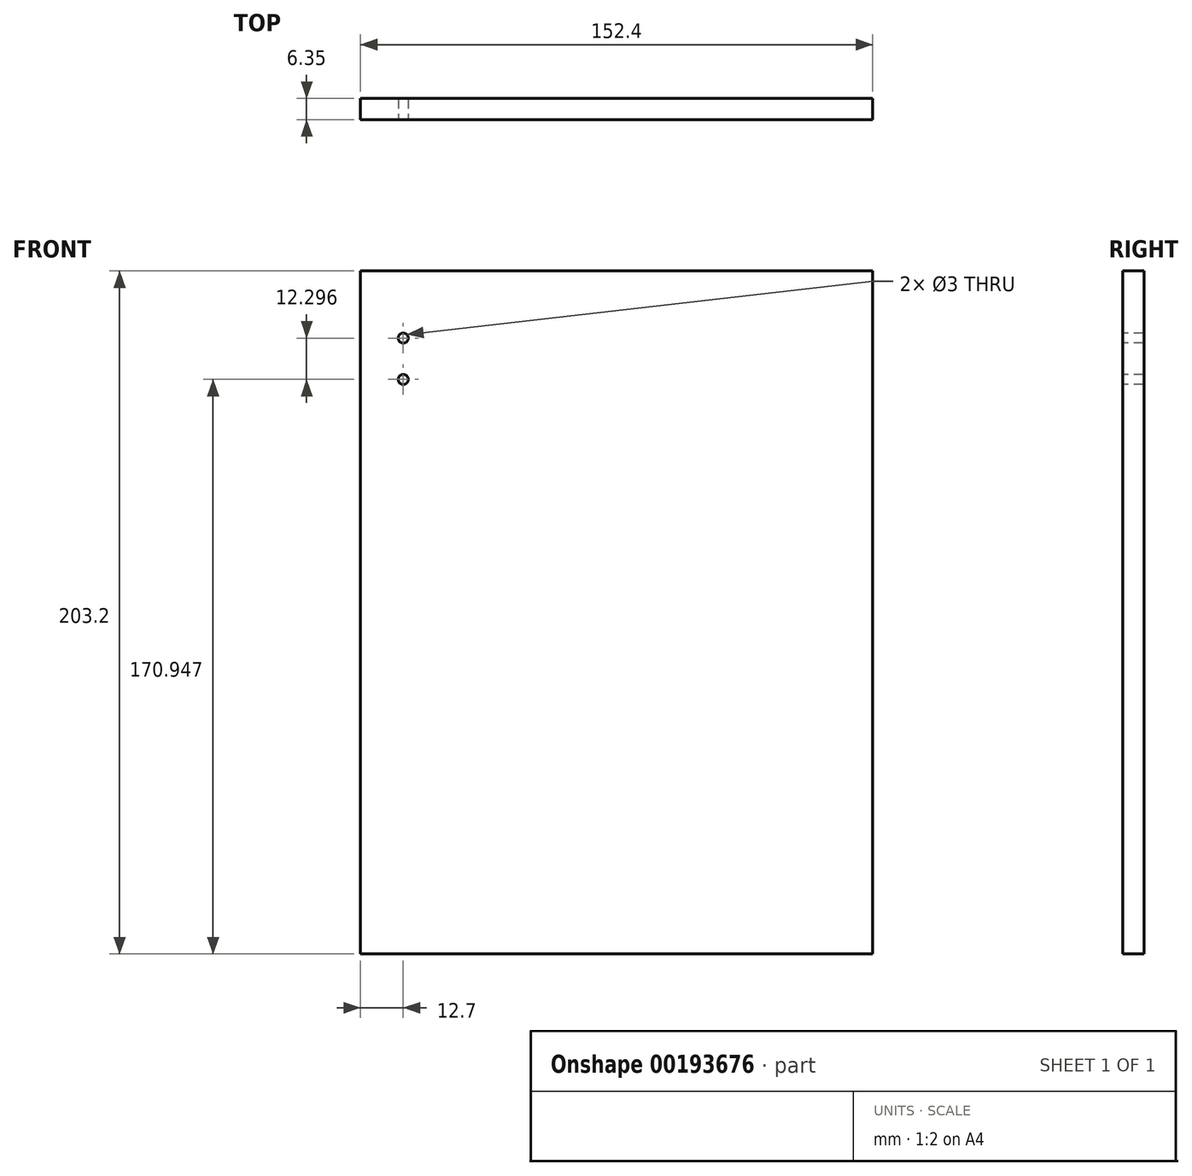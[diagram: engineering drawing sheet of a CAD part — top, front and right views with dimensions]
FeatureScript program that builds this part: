
annotation { "Feature Type Name" : "Feature", "Feature Type Description" : "" }
export const myFeature = defineFeature(function(context is Context, id is Id, definition is map)
    precondition{}
    {
        {
            var Q0;
            Q0=qCreatedBy(makeId("Front.planeOp"),FACE);
            var sketch = newSketch(context, id + "F0", { "sketchPlane" : qUnion([Q0])});
            skLineSegment(sketch, "E0.bottom", {"start": v(76.2, 101.6) * mm, "end": v(-76.2, 101.6) * mm});
            skLineSegment(sketch, "E0.top", {"start": v(76.2, -101.6) * mm, "end": v(-76.2, -101.6) * mm});
            skLineSegment(sketch, "E0.left", {"start": v(76.2, 101.6) * mm, "end": v(76.2, -101.6) * mm});
            skLineSegment(sketch, "E0.right", {"start": v(-76.2, 101.6) * mm, "end": v(-76.2, -101.6) * mm});
            skPoint(sketch, "E0.middle", {"position": v(0, 0) * mm});
            skSolve(sketch);
        }
        {
            var Q0;
            Q0=makeQuery(id+"F0.imprint","IMPRINT",FACE,{"disambiguationData":[TD([[makeQuery(id+"F0.imprint","IMPRINT",EDGE,{"derivedFrom":sQuery(id+"F0.wireOp",EDGE,"E0.bottom")}),1.0]])]});
            extrude(context, id + "F1", {"entities" : qUnion([Q0]), "depth" : 6.35 * mm});
        }
        {
            var Q0;
            Q0=makeQuery(id+"F1.opExtrude","CAP_FACE",FACE,{"disambiguationData":[OSD([sQuery(id+"F0.wireOp",EDGE,"E0.bottom"),sQuery(id+"F0.wireOp",EDGE,"E0.top"),sQuery(id+"F0.wireOp",EDGE,"E0.left"),sQuery(id+"F0.wireOp",EDGE,"E0.right")])],"isStart":false});
            var sketch = newSketch(context, id + "F2", { "sketchPlane" : qUnion([Q0])});
            skLineSegment(sketch, "E1", {"start": v(-63.5, 101.6) * mm, "end": v(-63.5, 82.55) * mm});
            skLineSegment(sketch, "E2", {"start": v(-63.5, 82.55) * mm, "end": v(-63.5, 69.85) * mm});
            skLineSegment(sketch, "E3", {"start": v(63.5, 101.6) * mm, "end": v(63.5, 82.55) * mm});
            skLineSegment(sketch, "E4", {"start": v(63.5, 82.55) * mm, "end": v(63.5, 69.85) * mm});
            skLineSegment(sketch, "E5", {"start": v(-63.5, -69.85) * mm, "end": v(-63.5, -82.55) * mm});
            skLineSegment(sketch, "E6", {"start": v(-63.5, -82.55) * mm, "end": v(-63.5, -101.6) * mm});
            skSolve(sketch);
        }
        {
            var Q0;
            {var subQ3=makeQuery(id+"F1.opExtrude","CAP_EDGE",EDGE,{"disambiguationData":[OSD([sQuery(id+"F0.wireOp",EDGE,"E0.left")])],"isStart":false});Q0=makeQuery(id+"F2.imprint","IMPRINT",FACE,{"disambiguationData":[TD([[makeQuery(id+"F2.imprint","IMPRINT",EDGE,{"derivedFrom":subQ3}),-1.0]])]});}
            var sketch = newSketch(context, id + "F3", { "sketchPlane" : qUnion([Q0])});
            skCircle(sketch, "E7", {"center": v(-63.5, 81.64) * mm, "radius": 1.5 * mm});
            skCircle(sketch, "E8", {"center": v(-63.5, 69.35) * mm, "radius": 1.5 * mm});
            skSolve(sketch);
        }
        {
            var Q0;
            Q0 = qSketchRegion(id + "F3", true);
            var Q1;
            Q1=makeQuery(id+"F1.opExtrude","CAP_FACE",FACE,{"disambiguationData":[OSD([sQuery(id+"F0.wireOp",EDGE,"E0.bottom"),sQuery(id+"F0.wireOp",EDGE,"E0.top"),sQuery(id+"F0.wireOp",EDGE,"E0.left"),sQuery(id+"F0.wireOp",EDGE,"E0.right")])],"isStart":true});
            extrude(context, id + "F4", {"entities" : qUnion([Q0, Q1]), "operationType" : NewBodyOperationType.REMOVE, "oppositeDirection" : true, "depth" : 76.2 * mm});
        }
    });
